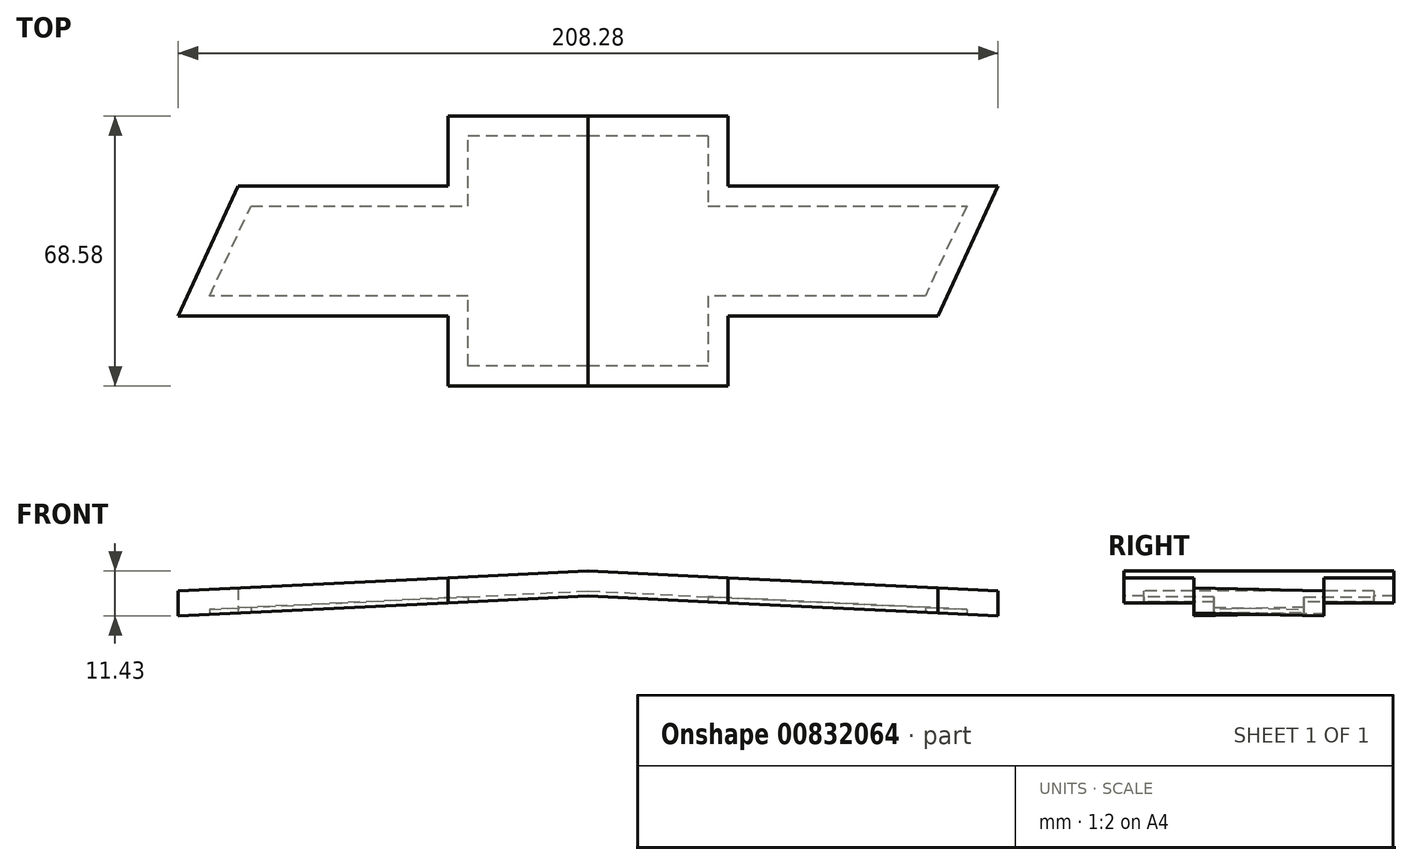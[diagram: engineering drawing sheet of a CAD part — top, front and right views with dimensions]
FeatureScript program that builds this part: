
annotation { "Feature Type Name" : "Feature", "Feature Type Description" : "" }
export const myFeature = defineFeature(function(context is Context, id is Id, definition is map)
    precondition{}
    {
        {
            var Q0;
            Q0=qCreatedBy(makeId("Top.planeOp"),FACE);
            var sketch = newSketch(context, id + "F0", { "sketchPlane" : qUnion([Q0])});
            skLineSegment(sketch, "E0", {"start": v(-98.43, 28.58) * mm, "end": v(-47.63, 28.58) * mm});
            skLineSegment(sketch, "E1", {"start": v(-47.63, 28.57) * mm, "end": v(-47.63, 47.63) * mm});
            skLineSegment(sketch, "E2", {"start": v(-47.63, 47.63) * mm, "end": v(47.63, 47.63) * mm});
            skLineSegment(sketch, "E3", {"start": v(47.63, 47.63) * mm, "end": v(47.63, 28.57) * mm});
            skLineSegment(sketch, "E4", {"start": v(47.63, 28.57) * mm, "end": v(123.83, 28.58) * mm});
            skLineSegment(sketch, "E5", {"start": v(123.83, 28.58) * mm, "end": v(98.43, -28.58) * mm});
            skLineSegment(sketch, "E6", {"start": v(98.43, -28.57) * mm, "end": v(47.63, -28.57) * mm});
            skLineSegment(sketch, "E7", {"start": v(47.63, -28.57) * mm, "end": v(47.63, -47.63) * mm});
            skLineSegment(sketch, "E8", {"start": v(47.63, -47.63) * mm, "end": v(-47.63, -47.63) * mm});
            skLineSegment(sketch, "E9", {"start": v(-47.63, -47.63) * mm, "end": v(-47.63, -28.57) * mm});
            skLineSegment(sketch, "E10", {"start": v(-47.63, -28.58) * mm, "end": v(-123.83, -28.58) * mm});
            skLineSegment(sketch, "E11", {"start": v(-123.83, -28.58) * mm, "end": v(-98.43, 28.58) * mm});
            skSolve(sketch);
        }
        {
            var Q0;
            Q0 = qSketchRegion(id + "F0", true);
            extrude(context, id + "F1", {"entities" : qUnion([Q0]), "depth" : 3 / 203.2 * mm, "offsetDistance" : 25.4 * mm});
        }
        {
            var Q0;
            Q0=makeQuery(id+"F1.opExtrude","CAP_FACE",FACE,{"disambiguationData":[OSD([sQuery(id+"F0.wireOp",EDGE,"E0"),sQuery(id+"F0.wireOp",EDGE,"E1"),sQuery(id+"F0.wireOp",EDGE,"E2"),sQuery(id+"F0.wireOp",EDGE,"E3"),sQuery(id+"F0.wireOp",EDGE,"E4"),sQuery(id+"F0.wireOp",EDGE,"E5"),sQuery(id+"F0.wireOp",EDGE,"E6"),sQuery(id+"F0.wireOp",EDGE,"E7"),sQuery(id+"F0.wireOp",EDGE,"E8"),sQuery(id+"F0.wireOp",EDGE,"E9"),sQuery(id+"F0.wireOp",EDGE,"E10"),sQuery(id+"F0.wireOp",EDGE,"E11")])],"isStart":false});
            var sketch = newSketch(context, id + "F2", { "sketchPlane" : qUnion([Q0])});
            skLineSegment(sketch, "E12.0", {"start": v(-36.2, 17.15) * mm, "end": v(-91, 17.15) * mm});
            skLineSegment(sketch, "E12.1", {"start": v(36.2, -36.2) * mm, "end": v(36.2, -17.14) * mm});
            skLineSegment(sketch, "E12.2", {"start": v(-36.2, -36.2) * mm, "end": v(36.2, -36.2) * mm});
            skLineSegment(sketch, "E12.3", {"start": v(-36.2, -17.15) * mm, "end": v(-36.2, -36.2) * mm});
            skLineSegment(sketch, "E12.4", {"start": v(-106.24, -17.15) * mm, "end": v(-36.2, -17.15) * mm});
            skLineSegment(sketch, "E12.5", {"start": v(36.2, -17.14) * mm, "end": v(91, -17.14) * mm});
            skLineSegment(sketch, "E12.6", {"start": v(-91, 17.15) * mm, "end": v(-106.24, -17.15) * mm});
            skLineSegment(sketch, "E12.7", {"start": v(91, -17.15) * mm, "end": v(106.24, 17.15) * mm});
            skLineSegment(sketch, "E12.8", {"start": v(106.24, 17.15) * mm, "end": v(36.2, 17.14) * mm});
            skLineSegment(sketch, "E12.9", {"start": v(36.2, 17.14) * mm, "end": v(36.2, 36.2) * mm});
            skLineSegment(sketch, "E12.10", {"start": v(36.2, 36.2) * mm, "end": v(-36.2, 36.2) * mm});
            skLineSegment(sketch, "E12.11", {"start": v(-36.2, 36.2) * mm, "end": v(-36.2, 17.15) * mm});
            skSolve(sketch);
        }
        {
            var Q0;
            Q0=makeQuery(id+"F2.imprint","IMPRINT",FACE,{"disambiguationData":[TD([[makeQuery(id+"F2.imprint","IMPRINT",EDGE,{"derivedFrom":sQuery(id+"F2.wireOp",EDGE,"E12.0")}),1.0]])]});
            extrude(context, id + "F3", {"entities" : qUnion([Q0]), "operationType" : NewBodyOperationType.REMOVE, "oppositeDirection" : true, "depth" : 6.35 * mm, "offsetDistance" : 25.4 * mm});
        }
        {
            var Q0;
            Q0=makeQuery(id+"F1.opExtrude","SWEPT_FACE",FACE,{"disambiguationData":[OSD([sQuery(id+"F0.wireOp",EDGE,"E8")])]});
            var sketch = newSketch(context, id + "F4", { "sketchPlane" : qUnion([Q0])});
            skLineSegment(sketch, "E13", {"start": v(-123.83, 3.81) * mm, "end": v(123.83, 3.81) * mm});
            skLineSegment(sketch, "E14", {"start": v(123.83, 3.81) * mm, "end": v(0, 8.9) * mm});
            skLineSegment(sketch, "E15", {"start": v(0, 8.9) * mm, "end": v(-123.83, 3.8) * mm});
            skSolve(sketch);
        }
        {
            var Q0;
            {var subQ0=sQuery(id+"F4.wireOp",EDGE,"E15");var subQ1=sQuery(id+"F4.wireOp",EDGE,"E14");var subQ2=makeQuery(id+"F4.imprint","INTERSECT",VERTEX,{"derivedFrom":[subQ1,subQ0]});Q0=makeQuery(id+"F4.imprint","IMPRINT",FACE,{"disambiguationData":[TD([[makeQuery(id+"F4.imprint","IMPRINT",EDGE,{"disambiguationData":[TD([[subQ2,1.0]])],"derivedFrom":subQ1}),1.0]])]});}
            var Q1;
            {var subQ0=sQuery(id+"F4.wireOp",EDGE,"E15");var subQ1=sQuery(id+"F4.wireOp",EDGE,"E13");var subQ2=makeQuery(id+"F4.imprint","INTERSECT",VERTEX,{"derivedFrom":[subQ1,subQ0]});Q1=makeQuery(id+"F4.imprint","IMPRINT",FACE,{"disambiguationData":[TD([[makeQuery(id+"F4.imprint","IMPRINT",EDGE,{"disambiguationData":[TD([[subQ2,-1.0]])],"derivedFrom":subQ1}),1.0]])]});}
            var Q2;
            {var subQ0=sQuery(id+"F4.wireOp",EDGE,"E14");var subQ1=sQuery(id+"F4.wireOp",EDGE,"E13");var subQ2=makeQuery(id+"F4.imprint","INTERSECT",VERTEX,{"derivedFrom":[subQ1,subQ0]});Q2=makeQuery(id+"F4.imprint","IMPRINT",FACE,{"disambiguationData":[TD([[makeQuery(id+"F4.imprint","IMPRINT",EDGE,{"disambiguationData":[TD([[subQ2,1.0]])],"derivedFrom":subQ1}),1.0]])]});}
            var Q3;
            Q3=makeQuery(id+"F3.boolean.opBoolean","COPY",FACE,{"derivedFrom":makeQuery(id+"F3.opExtrude","SWEPT_FACE",FACE,{"disambiguationData":[OSD([sQuery(id+"F2.wireOp",EDGE,"E12.10")])]})});
            extrude(context, id + "F5", {"entities" : qUnion([Q0, Q1, Q2]), "operationType" : NewBodyOperationType.ADD, "endBound" : BoundingType.UP_TO_SURFACE, "oppositeDirection" : true, "depth" : 76.2 * mm, "endBoundEntityFace" : qUnion([Q3]), "offsetDistance" : 25.4 * mm});
        }
        {
            var Q0;
            {var subQ1=sQuery(id+"F4.wireOp",EDGE,"E13");var subQ2=makeQuery(id+"F5.opExtrude","SWEPT_FACE",FACE,{"disambiguationData":[OSD([subQ1])]});Q0=makeQuery(id+"F5.boolean.opBoolean","SPLIT",FACE,{"disambiguationData":[TD([makeQuery(id+"F1.opExtrude","SWEPT_FACE",FACE,{"disambiguationData":[OSD([sQuery(id+"F0.wireOp",EDGE,"E9")])]})])],"derivedFrom":subQ2});}
            var Q1;
            {var subQ0=sQuery(id+"F4.wireOp",EDGE,"E13");var subQ1=makeQuery(id+"F5.opExtrude","SWEPT_FACE",FACE,{"disambiguationData":[OSD([subQ0])]});Q1=makeQuery(id+"F5.boolean.opBoolean","SPLIT",FACE,{"disambiguationData":[TD([makeQuery(id+"F1.opExtrude","SWEPT_FACE",FACE,{"disambiguationData":[OSD([sQuery(id+"F0.wireOp",EDGE,"E6")])]})])],"derivedFrom":subQ1});}
            var Q2;
            {var subQ0=makeQuery(id+"F5.opExtrude","SWEPT_FACE",FACE,{"disambiguationData":[OSD([sQuery(id+"F4.wireOp",EDGE,"E13")])]});Q2=makeQuery(id+"F5.boolean.opBoolean","SPLIT",FACE,{"disambiguationData":[TD([makeQuery(id+"F1.opExtrude","SWEPT_FACE",FACE,{"disambiguationData":[OSD([sQuery(id+"F0.wireOp",EDGE,"E3")])]})])],"derivedFrom":subQ0});}
            var Q3;
            {var subQ0=makeQuery(id+"F5.opExtrude","SWEPT_FACE",FACE,{"disambiguationData":[OSD([sQuery(id+"F4.wireOp",EDGE,"E13")])]});Q3=makeQuery(id+"F5.boolean.opBoolean","SPLIT",FACE,{"disambiguationData":[TD([makeQuery(id+"F1.opExtrude","SWEPT_FACE",FACE,{"disambiguationData":[OSD([sQuery(id+"F0.wireOp",EDGE,"E0")])]})])],"derivedFrom":subQ0});}
            extrude(context, id + "F6", {"entities" : qUnion([Q0, Q1, Q2, Q3]), "operationType" : NewBodyOperationType.REMOVE, "endBound" : BoundingType.UP_TO_NEXT, "oppositeDirection" : true, "depth" : 25.4 * mm, "offsetDistance" : 25.4 * mm});
        }
        {
            var Q0;
            Q0=makeQuery(id+"F1.opExtrude","CAP_EDGE",EDGE,{"disambiguationData":[OSD([sQuery(id+"F0.wireOp",EDGE,"E11")])],"isStart":false});
            var Q1;
            Q1=makeQuery(id+"F1.opExtrude","CAP_EDGE",EDGE,{"disambiguationData":[OSD([sQuery(id+"F0.wireOp",EDGE,"E0")])],"isStart":false});
            var Q2;
            Q2=makeQuery(id+"F1.opExtrude","CAP_EDGE",EDGE,{"disambiguationData":[OSD([sQuery(id+"F0.wireOp",EDGE,"E2")])],"isStart":false});
            var Q3;
            Q3=makeQuery(id+"F1.opExtrude","CAP_EDGE",EDGE,{"disambiguationData":[OSD([sQuery(id+"F0.wireOp",EDGE,"E1")])],"isStart":false});
            var Q4;
            Q4=makeQuery(id+"F1.opExtrude","CAP_EDGE",EDGE,{"disambiguationData":[OSD([sQuery(id+"F0.wireOp",EDGE,"E3")])],"isStart":false});
            var Q5;
            Q5=makeQuery(id+"F1.opExtrude","CAP_EDGE",EDGE,{"disambiguationData":[OSD([sQuery(id+"F0.wireOp",EDGE,"E4")])],"isStart":false});
            var Q6;
            Q6=makeQuery(id+"F1.opExtrude","CAP_EDGE",EDGE,{"disambiguationData":[OSD([sQuery(id+"F0.wireOp",EDGE,"E5")])],"isStart":false});
            var Q7;
            Q7=makeQuery(id+"F1.opExtrude","CAP_EDGE",EDGE,{"disambiguationData":[OSD([sQuery(id+"F0.wireOp",EDGE,"E6")])],"isStart":false});
            var Q8;
            Q8=makeQuery(id+"F1.opExtrude","CAP_EDGE",EDGE,{"disambiguationData":[OSD([sQuery(id+"F0.wireOp",EDGE,"E7")])],"isStart":false});
            var Q9;
            Q9=makeQuery(id+"F1.opExtrude","CAP_EDGE",EDGE,{"disambiguationData":[OSD([sQuery(id+"F0.wireOp",EDGE,"E8")])],"isStart":false});
            var Q10;
            Q10=makeQuery(id+"F1.opExtrude","CAP_EDGE",EDGE,{"disambiguationData":[OSD([sQuery(id+"F0.wireOp",EDGE,"E9")])],"isStart":false});
            var Q11;
            Q11=makeQuery(id+"F1.opExtrude","CAP_EDGE",EDGE,{"disambiguationData":[OSD([sQuery(id+"F0.wireOp",EDGE,"E10")])],"isStart":false});
            chamfer(context, id + "F7", {"entities" : qUnion([Q0, Q1, Q2, Q3, Q4, Q5, Q6, Q7, Q8, Q9, Q10, Q11]), "width" : 9.52 * mm, "tangentPropagation" : true});
        }
        {
            var Q0;
            Q0=qCreatedBy(makeId("Top.planeOp"),FACE);
            var sketch = newSketch(context, id + "F8", { "sketchPlane" : qUnion([Q0])});
            skLineSegment(sketch, "E16", {"start": v(-88.9, -106.68) * mm, "end": v(-35.56, -106.68) * mm});
            skLineSegment(sketch, "E17", {"start": v(-35.56, -106.68) * mm, "end": v(-35.56, -88.9) * mm});
            skLineSegment(sketch, "E18", {"start": v(-35.56, -88.9) * mm, "end": v(35.56, -88.9) * mm});
            skLineSegment(sketch, "E19", {"start": v(35.56, -88.9) * mm, "end": v(35.56, -106.68) * mm});
            skLineSegment(sketch, "E20", {"start": v(35.56, -106.68) * mm, "end": v(104.14, -106.68) * mm});
            skLineSegment(sketch, "E21", {"start": v(104.14, -106.68) * mm, "end": v(88.9, -139.7) * mm});
            skLineSegment(sketch, "E22", {"start": v(88.9, -139.7) * mm, "end": v(35.56, -139.7) * mm});
            skLineSegment(sketch, "E23", {"start": v(35.56, -139.7) * mm, "end": v(35.56, -157.48) * mm});
            skLineSegment(sketch, "E24", {"start": v(35.56, -157.48) * mm, "end": v(-35.56, -157.48) * mm});
            skLineSegment(sketch, "E25", {"start": v(-35.56, -157.48) * mm, "end": v(-35.56, -139.7) * mm});
            skLineSegment(sketch, "E26", {"start": v(-35.56, -139.7) * mm, "end": v(-104.14, -139.7) * mm});
            skLineSegment(sketch, "E27", {"start": v(-104.14, -139.7) * mm, "end": v(-88.9, -106.68) * mm});
            skSolve(sketch);
        }
        {
            var Q0;
            Q0 = qSketchRegion(id + "F8", true);
            extrude(context, id + "F9", {"entities" : qUnion([Q0]), "depth" : 6.35 * mm, "offsetDistance" : 25.4 * mm});
        }
        {
            var Q0;
            Q0=makeQuery(id+"F9.opExtrude","SWEPT_FACE",FACE,{"disambiguationData":[OSD([sQuery(id+"F8.wireOp",EDGE,"E24")])]});
            var sketch = newSketch(context, id + "F10", { "sketchPlane" : qUnion([Q0])});
            skLineSegment(sketch, "E28", {"start": v(-104.14, 6.35) * mm, "end": v(0, 11.43) * mm});
            skLineSegment(sketch, "E29", {"start": v(0, 11.43) * mm, "end": v(104.14, 6.35) * mm});
            skLineSegment(sketch, "E30", {"start": v(104.14, 6.35) * mm, "end": v(-104.14, 6.35) * mm});
            skSolve(sketch);
        }
        {
            var Q0;
            Q0 = qSketchRegion(id + "F10", true);
            var Q1;
            Q1=makeQuery(id+"F9.opExtrude","SWEPT_FACE",FACE,{"disambiguationData":[OSD([sQuery(id+"F8.wireOp",EDGE,"E18")])]});
            extrude(context, id + "F11", {"entities" : qUnion([Q0]), "operationType" : NewBodyOperationType.ADD, "endBound" : BoundingType.UP_TO_SURFACE, "oppositeDirection" : true, "depth" : 25.4 * mm, "endBoundEntityFace" : qUnion([Q1]), "offsetDistance" : 25.4 * mm});
        }
        {
            var Q0;
            {var subQ1=sQuery(id+"F10.wireOp",EDGE,"E30");var subQ2=makeQuery(id+"F11.opExtrude","SWEPT_FACE",FACE,{"disambiguationData":[OSD([subQ1])]});Q0=makeQuery(id+"F11.boolean.opBoolean","SPLIT",FACE,{"disambiguationData":[TD([makeQuery(id+"F9.opExtrude","SWEPT_FACE",FACE,{"disambiguationData":[OSD([sQuery(id+"F8.wireOp",EDGE,"E25")])]})])],"derivedFrom":subQ2});}
            var Q1;
            {var subQ1=makeQuery(id+"F11.opExtrude","SWEPT_FACE",FACE,{"disambiguationData":[OSD([sQuery(id+"F10.wireOp",EDGE,"E30")])]});Q1=makeQuery(id+"F11.boolean.opBoolean","SPLIT",FACE,{"disambiguationData":[TD([makeQuery(id+"F9.opExtrude","SWEPT_FACE",FACE,{"disambiguationData":[OSD([sQuery(id+"F8.wireOp",EDGE,"E16")])]})])],"derivedFrom":subQ1});}
            var Q2;
            {var subQ0=sQuery(id+"F10.wireOp",EDGE,"E30");var subQ2=makeQuery(id+"F11.opExtrude","SWEPT_FACE",FACE,{"disambiguationData":[OSD([subQ0])]});Q2=makeQuery(id+"F11.boolean.opBoolean","SPLIT",FACE,{"disambiguationData":[TD([makeQuery(id+"F9.opExtrude","SWEPT_FACE",FACE,{"disambiguationData":[OSD([sQuery(id+"F8.wireOp",EDGE,"E22")])]})])],"derivedFrom":subQ2});}
            var Q3;
            {var subQ0=makeQuery(id+"F11.opExtrude","SWEPT_FACE",FACE,{"disambiguationData":[OSD([sQuery(id+"F10.wireOp",EDGE,"E30")])]});Q3=makeQuery(id+"F11.boolean.opBoolean","SPLIT",FACE,{"disambiguationData":[TD([makeQuery(id+"F9.opExtrude","SWEPT_FACE",FACE,{"disambiguationData":[OSD([sQuery(id+"F8.wireOp",EDGE,"E19")])]})])],"derivedFrom":subQ0});}
            extrude(context, id + "F12", {"entities" : qUnion([Q0, Q1, Q2, Q3]), "operationType" : NewBodyOperationType.REMOVE, "endBound" : BoundingType.UP_TO_NEXT, "oppositeDirection" : true, "depth" : 25.4 * mm, "offsetDistance" : 25.4 * mm});
        }
        {
            var Q0;
            Q0=makeQuery(id+"F11.boolean.opBoolean","MERGE",FACE,{"derivedFrom":[makeQuery(id+"F9.opExtrude","SWEPT_FACE",FACE,{"disambiguationData":[OSD([sQuery(id+"F8.wireOp",EDGE,"E24")])]}),makeQuery(id+"F11.opExtrude","CAP_FACE",FACE,{"disambiguationData":[OSD([sQuery(id+"F10.wireOp",EDGE,"E28"),sQuery(id+"F10.wireOp",EDGE,"E29"),sQuery(id+"F10.wireOp",EDGE,"E30")])],"isStart":true})]});
            var sketch = newSketch(context, id + "F13", { "sketchPlane" : qUnion([Q0])});
            skLineSegment(sketch, "E31", {"start": v(-104.14, 0) * mm, "end": v(104.14, 0) * mm});
            skLineSegment(sketch, "E32", {"start": v(104.14, 0) * mm, "end": v(0, 5.08) * mm});
            skLineSegment(sketch, "E33", {"start": v(0, 5.08) * mm, "end": v(-104.14, 0) * mm});
            skSolve(sketch);
        }
        {
            var Q0;
            Q0 = qSketchRegion(id + "F13", true);
            var Q1;
            {var subQ0=sQuery(id+"F8.wireOp",EDGE,"E18");Q1=makeQuery(id+"F11.boolean.opBoolean","MERGE",FACE,{"derivedFrom":[makeQuery(id+"F9.opExtrude","SWEPT_FACE",FACE,{"disambiguationData":[OSD([subQ0])]}),makeQuery(id+"F11.opExtrude","CAP_FACE",FACE,{"disambiguationData":[OSD([subQ0])],"isStart":false})]});}
            extrude(context, id + "F14", {"entities" : qUnion([Q0]), "operationType" : NewBodyOperationType.REMOVE, "endBound" : BoundingType.UP_TO_SURFACE, "oppositeDirection" : true, "depth" : 25.4 * mm, "endBoundEntityFace" : qUnion([Q1]), "offsetDistance" : 25.4 * mm});
        }
        {
            var Q0;
            Q0=makeQuery(id+"F14.boolean.opBoolean","COPY",FACE,{"derivedFrom":makeQuery(id+"F14.opExtrude","SWEPT_FACE",FACE,{"disambiguationData":[OSD([sQuery(id+"F13.wireOp",EDGE,"E33")])]})});
            var Q1;
            Q1=makeQuery(id+"F14.boolean.opBoolean","COPY",FACE,{"derivedFrom":makeQuery(id+"F14.opExtrude","SWEPT_FACE",FACE,{"disambiguationData":[OSD([sQuery(id+"F13.wireOp",EDGE,"E32")])]})});
            shell(context, id + "F15", {"entities" : qUnion([Q0, Q1]), "thickness" : 5.08 * mm});
        }
        {
            var Q0;
            Q0=makeQuery(id+"F1.opExtrude","CAP_FACE",FACE,{"disambiguationData":[OSD([sQuery(id+"F0.wireOp",EDGE,"E0"),sQuery(id+"F0.wireOp",EDGE,"E1"),sQuery(id+"F0.wireOp",EDGE,"E2"),sQuery(id+"F0.wireOp",EDGE,"E3"),sQuery(id+"F0.wireOp",EDGE,"E4"),sQuery(id+"F0.wireOp",EDGE,"E5"),sQuery(id+"F0.wireOp",EDGE,"E6"),sQuery(id+"F0.wireOp",EDGE,"E7"),sQuery(id+"F0.wireOp",EDGE,"E8"),sQuery(id+"F0.wireOp",EDGE,"E9"),sQuery(id+"F0.wireOp",EDGE,"E10"),sQuery(id+"F0.wireOp",EDGE,"E11")])],"isStart":true});
            var sketch = newSketch(context, id + "F16", { "sketchPlane" : qUnion([Q0])});
            skLineSegment(sketch, "E34.0", {"start": v(-41.28, 22.23) * mm, "end": v(-114.05, 22.23) * mm});
            skLineSegment(sketch, "E34.1", {"start": v(41.28, -41.28) * mm, "end": v(41.28, -22.23) * mm});
            skLineSegment(sketch, "E34.2", {"start": v(-41.28, -41.28) * mm, "end": v(41.28, -41.28) * mm});
            skLineSegment(sketch, "E34.3", {"start": v(-41.28, -22.23) * mm, "end": v(-41.28, -41.28) * mm});
            skLineSegment(sketch, "E34.4", {"start": v(-94.3, -22.23) * mm, "end": v(-41.28, -22.23) * mm});
            skLineSegment(sketch, "E34.5", {"start": v(41.28, -22.22) * mm, "end": v(114.05, -22.23) * mm});
            skLineSegment(sketch, "E34.6", {"start": v(-114.05, 22.23) * mm, "end": v(-94.3, -22.23) * mm});
            skLineSegment(sketch, "E34.7", {"start": v(114.05, -22.23) * mm, "end": v(94.3, 22.23) * mm});
            skLineSegment(sketch, "E34.8", {"start": v(94.3, 22.22) * mm, "end": v(41.28, 22.23) * mm});
            skLineSegment(sketch, "E34.9", {"start": v(41.28, 22.23) * mm, "end": v(41.28, 41.28) * mm});
            skLineSegment(sketch, "E34.10", {"start": v(41.28, 41.28) * mm, "end": v(-41.28, 41.28) * mm});
            skLineSegment(sketch, "E34.11", {"start": v(-41.28, 41.28) * mm, "end": v(-41.28, 22.23) * mm});
            skSolve(sketch);
        }
        {
            var Q0;
            Q0 = qSketchRegion(id + "F16", true);
            extrude(context, id + "F17", {"entities" : qUnion([Q0]), "operationType" : NewBodyOperationType.REMOVE, "oppositeDirection" : true, "depth" : 2.54 * mm, "offsetDistance" : 25.4 * mm});
        }
    });
